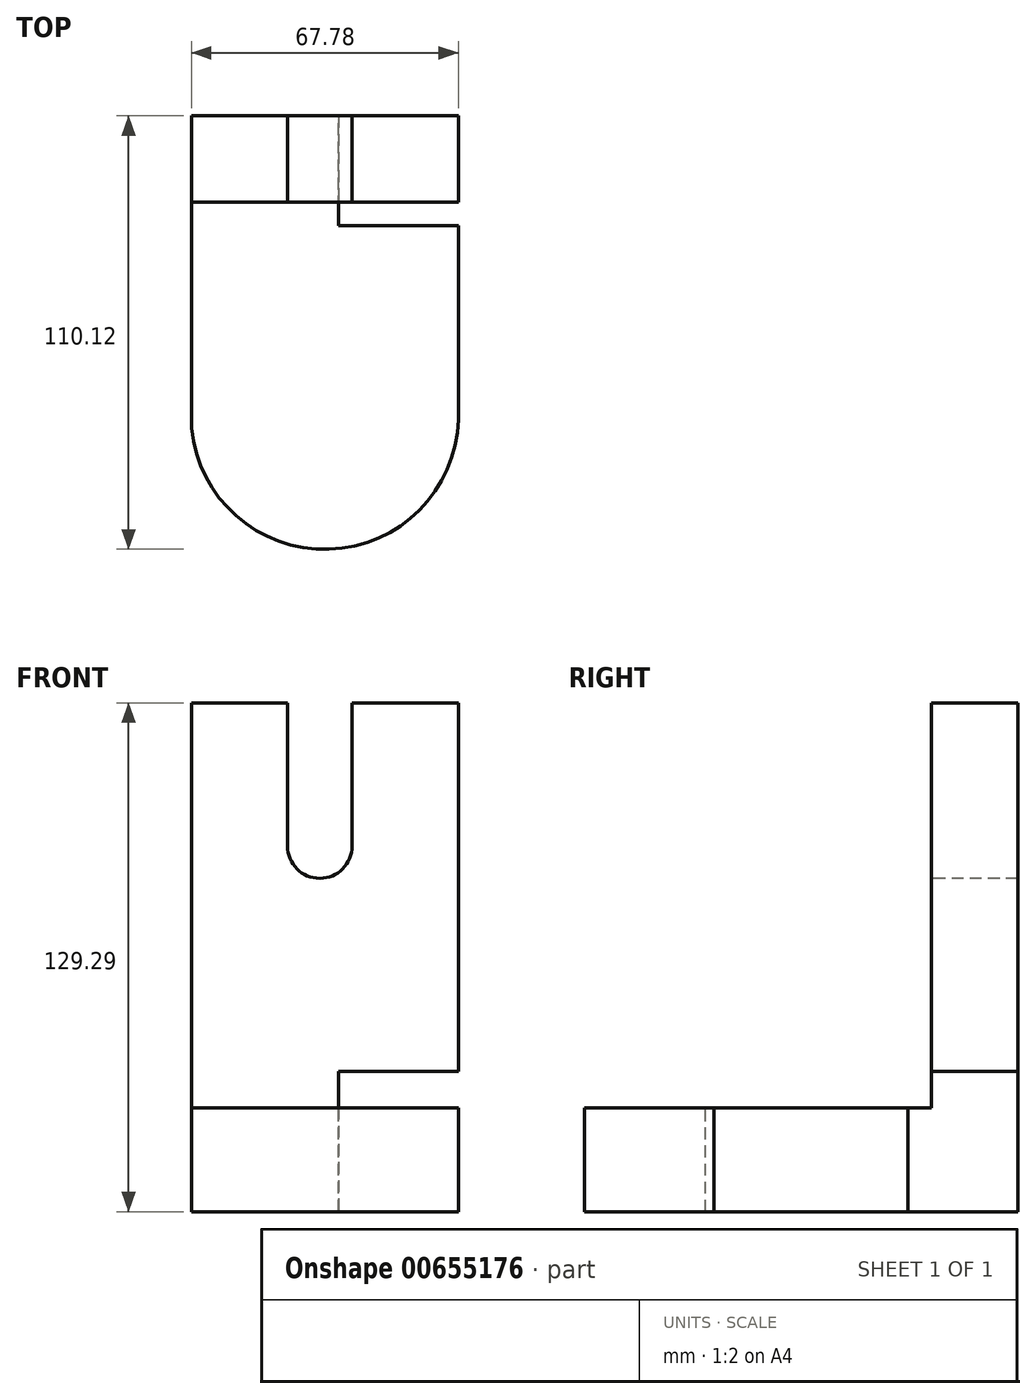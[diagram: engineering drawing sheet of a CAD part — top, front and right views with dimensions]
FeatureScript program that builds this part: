
annotation { "Feature Type Name" : "Feature", "Feature Type Description" : "" }
export const myFeature = defineFeature(function(context is Context, id is Id, definition is map)
    precondition{}
    {
        {
            var Q0;
            Q0=qCreatedBy(makeId("Top.planeOp"),FACE);
            var sketch = newSketch(context, id + "F0", { "sketchPlane" : qUnion([Q0])});
            skLineSegment(sketch, "E0.bottom", {"start": v(33.89, 55.12) * mm, "end": v(-33.89, 55.12) * mm});
            skLineSegment(sketch, "E0.top", {"start": v(33.89, -55.12) * mm, "end": v(-33.89, -55.12) * mm});
            skLineSegment(sketch, "E0.left", {"start": v(33.89, 55.12) * mm, "end": v(33.89, -55.12) * mm});
            skLineSegment(sketch, "E0.right", {"start": v(-33.89, 55.12) * mm, "end": v(-33.89, -55.12) * mm});
            skPoint(sketch, "E0.middle", {"position": v(0, 0) * mm});
            skSolve(sketch);
        }
        {
            var Q0;
            Q0 = qSketchRegion(id + "F0", true);
            extrude(context, id + "F1", {"entities" : qUnion([Q0]), "depth" : 10.67 * mm, "offsetDistance" : 25.4 * mm});
        }
        {
            var Q0;
            Q0=makeQuery(id+"F1.opExtrude","CAP_FACE",FACE,{"disambiguationData":[OSD([sQuery(id+"F0.wireOp",EDGE,"E0.bottom"),sQuery(id+"F0.wireOp",EDGE,"E0.top"),sQuery(id+"F0.wireOp",EDGE,"E0.left"),sQuery(id+"F0.wireOp",EDGE,"E0.right")])],"isStart":false});
            var sketch = newSketch(context, id + "F2", { "sketchPlane" : qUnion([Q0])});
            skLineSegment(sketch, "E1.bottom", {"start": v(-33.89, 55.12) * mm, "end": v(33.89, 55.12) * mm});
            skLineSegment(sketch, "E1.top", {"start": v(-33.89, 33.14) * mm, "end": v(33.89, 33.14) * mm});
            skLineSegment(sketch, "E1.left", {"start": v(-33.89, 55.12) * mm, "end": v(-33.89, 33.14) * mm});
            skLineSegment(sketch, "E1.right", {"start": v(33.89, 55.12) * mm, "end": v(33.89, 33.14) * mm});
            skSolve(sketch);
        }
        {
            var Q0;
            Q0=makeQuery(id+"F2.imprint","IMPRINT",FACE,{"disambiguationData":[TD([[makeQuery(id+"F2.imprint","IMPRINT",EDGE,{"derivedFrom":sQuery(id+"F2.wireOp",EDGE,"E1.bottom")}),1.0]])]});
            extrude(context, id + "F3", {"entities" : qUnion([Q0]), "operationType" : NewBodyOperationType.ADD, "depth" : 84.07 * mm, "offsetDistance" : 25.4 * mm});
        }
        {
            var Q0;
            Q0=makeQuery(id+"F1.opExtrude","CAP_FACE",FACE,{"disambiguationData":[OSD([sQuery(id+"F0.wireOp",EDGE,"E0.bottom"),sQuery(id+"F0.wireOp",EDGE,"E0.top"),sQuery(id+"F0.wireOp",EDGE,"E0.left"),sQuery(id+"F0.wireOp",EDGE,"E0.right")])],"isStart":false});
            extrude(context, id + "F4", {"entities" : qUnion([Q0]), "operationType" : NewBodyOperationType.ADD, "depth" : 15.75 * mm, "offsetDistance" : 25.4 * mm});
        }
        {
            var Q0;
            Q0=makeQuery(id+"F3.opExtrude","CAP_FACE",FACE,{"disambiguationData":[OSD([sQuery(id+"F2.wireOp",EDGE,"E1.bottom"),sQuery(id+"F2.wireOp",EDGE,"E1.top"),sQuery(id+"F2.wireOp",EDGE,"E1.left"),sQuery(id+"F2.wireOp",EDGE,"E1.right")])],"isStart":false});
            extrude(context, id + "F5", {"entities" : qUnion([Q0]), "operationType" : NewBodyOperationType.ADD, "depth" : 34.54 * mm, "offsetDistance" : 25.4 * mm});
        }
        {
            var Q0;
            {var subQ0=sQuery(id+"F2.wireOp",EDGE,"E1.top");Q0=makeQuery(id+"F5.boolean.opBoolean","MERGE",FACE,{"derivedFrom":[makeQuery(id+"F3.opExtrude","SWEPT_FACE",FACE,{"disambiguationData":[OSD([subQ0])]}),makeQuery(id+"F5.opExtrude","SWEPT_FACE",FACE,{"disambiguationData":[OSD([subQ0])]})]});}
            var sketch = newSketch(context, id + "F6", { "sketchPlane" : qUnion([Q0])});
            skLineSegment(sketch, "E2.left", {"start": v(-9.55, 129.29) * mm, "end": v(-9.55, 92.93) * mm});
            skLineSegment(sketch, "E2.right", {"start": v(6.9, 129.29) * mm, "end": v(6.9, 92.93) * mm});
            skArc(sketch, "E3", {"start": v(-9.55, 92.93) * mm, "mid": v(-1.32, 84.7) * mm, "end": v(6.9, 92.93) * mm});
            skSolve(sketch);
        }
        {
            var Q0;
            {var subQ0=sQuery(id+"F6.wireOp",EDGE,"E2.left");Q0=makeQuery(id+"F6.imprint","IMPRINT",FACE,{"disambiguationData":[TD([[makeQuery(id+"F6.imprint","IMPRINT",EDGE,{"derivedFrom":subQ0}),1.0]])]});}
            extrude(context, id + "F7", {"entities" : qUnion([Q0]), "operationType" : NewBodyOperationType.REMOVE, "oppositeDirection" : true, "depth" : 25.4 * mm, "offsetDistance" : 25.4 * mm});
        }
        {
            var Q0;
            Q0=makeQuery(id+"F4.opExtrude","CAP_FACE",FACE,{"disambiguationData":[OSD([sQuery(id+"F0.wireOp",EDGE,"E0.bottom"),sQuery(id+"F0.wireOp",EDGE,"E0.top"),sQuery(id+"F0.wireOp",EDGE,"E0.left"),sQuery(id+"F0.wireOp",EDGE,"E0.right")])],"isStart":false});
            var sketch = newSketch(context, id + "F8", { "sketchPlane" : qUnion([Q0])});
            skArc(sketch, "E4", {"start": v(-33.89, -17.88) * mm, "mid": v(-1.13, -54.98) * mm, "end": v(33.89, -20) * mm});
            skSolve(sketch);
        }
        {
            var Q0;
            {var subQ5=makeQuery(id+"F4.opExtrude","CAP_EDGE",EDGE,{"disambiguationData":[OSD([sQuery(id+"F0.wireOp",EDGE,"E0.top")])],"isStart":false});Q0=makeQuery(id+"F8.imprint","IMPRINT",FACE,{"disambiguationData":[TD([[makeQuery(id+"F8.imprint","IMPRINT",EDGE,{"derivedFrom":subQ5}),-1.0]])]});}
            extrude(context, id + "F9", {"entities" : qUnion([Q0]), "operationType" : NewBodyOperationType.REMOVE, "oppositeDirection" : true, "depth" : 64.77 * mm, "offsetDistance" : 25.4 * mm});
        }
        {
            var Q0;
            {var subQ0=sQuery(id+"F2.wireOp",EDGE,"E1.right");var subQ1=sQuery(id+"F0.wireOp",EDGE,"E0.left");Q0=makeQuery(id+"F5.boolean.opBoolean","MERGE",FACE,{"derivedFrom":[makeQuery(id+"F4.boolean.opBoolean","MERGE",FACE,{"derivedFrom":[makeQuery(id+"F3.boolean.opBoolean","MERGE",FACE,{"derivedFrom":[makeQuery(id+"F1.opExtrude","SWEPT_FACE",FACE,{"disambiguationData":[OSD([subQ1])]}),makeQuery(id+"F3.opExtrude","SWEPT_FACE",FACE,{"disambiguationData":[OSD([subQ0])]})]}),makeQuery(id+"F4.opExtrude","SWEPT_FACE",FACE,{"disambiguationData":[OSD([subQ1])]})]}),makeQuery(id+"F5.opExtrude","SWEPT_FACE",FACE,{"disambiguationData":[OSD([subQ0])]})]});}
            var sketch = newSketch(context, id + "F10", { "sketchPlane" : qUnion([Q0])});
            skLineSegment(sketch, "E5.bottom", {"start": v(59.53, 35.62) * mm, "end": v(27.22, 35.62) * mm});
            skLineSegment(sketch, "E5.top", {"start": v(59.53, -5.15) * mm, "end": v(27.22, -5.15) * mm});
            skLineSegment(sketch, "E5.left", {"start": v(59.53, 35.62) * mm, "end": v(59.53, -5.15) * mm});
            skLineSegment(sketch, "E5.right", {"start": v(27.22, 35.62) * mm, "end": v(27.22, -5.15) * mm});
            skPoint(sketch, "E5.middle", {"position": v(43.38, 15.23) * mm});
            skSolve(sketch);
        }
        {
            var Q0;
            Q0 = qSketchRegion(id + "F10", true);
            extrude(context, id + "F11", {"entities" : qUnion([Q0]), "operationType" : NewBodyOperationType.REMOVE, "oppositeDirection" : true, "depth" : 30.48 * mm, "offsetDistance" : 25.4 * mm});
        }
    });
